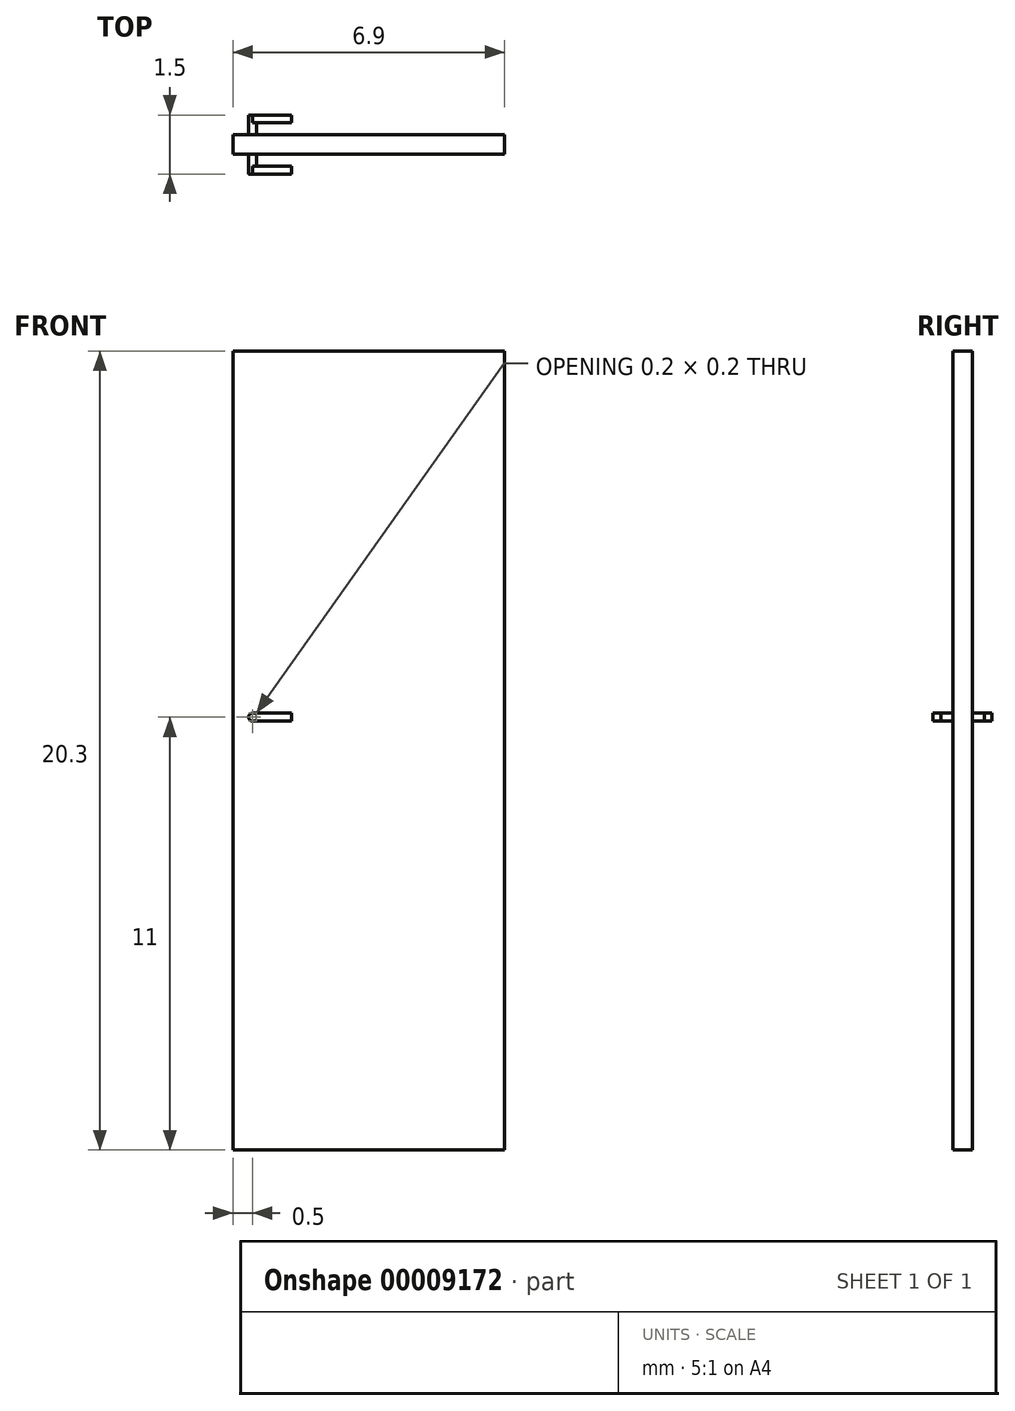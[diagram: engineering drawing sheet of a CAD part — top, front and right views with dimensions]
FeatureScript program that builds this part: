
annotation { "Feature Type Name" : "Feature", "Feature Type Description" : "" }
export const myFeature = defineFeature(function(context is Context, id is Id, definition is map)
    precondition{}
    {
        {
            var Q0;
            Q0=qCreatedBy(makeId("Top.planeOp"),FACE);
            var sketch = newSketch(context, id + "F0", { "sketchPlane" : qUnion([Q0])});
            skLineSegment(sketch, "E0.rect.bottom", {"start": v(3.45, 0.25) * mm, "end": v(-3.45, 0.25) * mm});
            skLineSegment(sketch, "E0.rect.top", {"start": v(3.45, -0.25) * mm, "end": v(-3.45, -0.25) * mm});
            skLineSegment(sketch, "E0.rect.left", {"start": v(3.45, 0.25) * mm, "end": v(3.45, -0.25) * mm});
            skLineSegment(sketch, "E0.rect.right", {"start": v(-3.45, 0.25) * mm, "end": v(-3.45, -0.25) * mm});
            skPoint(sketch, "E0.rect.middle", {"position": v(0, 0) * mm});
            skSolve(sketch);
        }
        {
            var Q0;
            Q0 = qSketchRegion(id + "F0", true);
            extrude(context, id + "F1", {"entities" : qUnion([Q0]), "depth" : 20.3 * mm});
        }
        {
            var Q0;
            Q0=makeQuery(id+"F1.opExtrude","SWEPT_FACE",FACE,{"disambiguationData":[OSD([sQuery(id+"F0.wireOp",EDGE,"E0.rect.top")])]});
            var sketch = newSketch(context, id + "F2", { "sketchPlane" : qUnion([Q0])});
            skCircle(sketch, "E1", {"center": v(-2.95, 11) * mm, "radius": 0.1 * mm});
            skSolve(sketch);
        }
        {
            var Q0;
            Q0 = qSketchRegion(id + "F2", true);
            extrude(context, id + "F3", {"entities" : qUnion([Q0]), "operationType" : NewBodyOperationType.ADD, "depth" : 0.5 * mm});
        }
        {
            var Q0;
            Q0=makeQuery(id+"F3.opExtrude","CAP_FACE",FACE,{"disambiguationData":[OSD([sQuery(id+"F2.wireOp",EDGE,"E1")])],"isStart":false});
            var sketch = newSketch(context, id + "F4", { "sketchPlane" : qUnion([Q0])});
            skLineSegment(sketch, "E2.bottom", {"start": v(-2.95, 11.1) * mm, "end": v(-1.95, 11.1) * mm});
            skLineSegment(sketch, "E2.top", {"start": v(-2.95, 10.9) * mm, "end": v(-1.95, 10.9) * mm});
            skLineSegment(sketch, "E2.left", {"start": v(-2.95, 11.1) * mm, "end": v(-2.95, 10.9) * mm});
            skLineSegment(sketch, "E2.right", {"start": v(-1.95, 11.1) * mm, "end": v(-1.95, 10.9) * mm});
            skSolve(sketch);
        }
        {
            var Q0;
            Q0 = qSketchRegion(id + "F4", true);
            extrude(context, id + "F5", {"entities" : qUnion([Q0]), "operationType" : NewBodyOperationType.ADD, "oppositeDirection" : true, "depth" : 0.2 * mm});
        }
        {
            var Q0;
            Q0=qCreatedBy(makeId("Front.planeOp"),FACE);
            var sketch = newSketch(context, id + "F6", { "sketchPlane" : qUnion([Q0])});
            skLineSegment(sketch, "E3.bottom", {"start": v(-16.2, 19.87) * mm, "end": v(-59.47, 19.87) * mm});
            skLineSegment(sketch, "E3.top", {"start": v(-16.2, -21.93) * mm, "end": v(-59.47, -21.93) * mm});
            skLineSegment(sketch, "E3.left", {"start": v(-16.2, 19.87) * mm, "end": v(-16.2, -21.93) * mm});
            skLineSegment(sketch, "E3.right", {"start": v(-59.47, 19.87) * mm, "end": v(-59.47, -21.93) * mm});
            skSolve(sketch);
        }
        {
            var Q0;
            Q0=makeQuery(id+"F1.opExtrude","SWEPT_BODY",BODY,{"disambiguationData":[OSD([sQuery(id+"F0.wireOp",EDGE,"E0.rect.bottom"),sQuery(id+"F0.wireOp",EDGE,"E0.rect.top"),sQuery(id+"F0.wireOp",EDGE,"E0.rect.left"),sQuery(id+"F0.wireOp",EDGE,"E0.rect.right")])]});
            var Q1;
            Q1=makeQuery(id+"F6.imprint","IMPRINT",FACE,{"disambiguationData":[TD([[makeQuery(id+"F6.imprint","IMPRINT",EDGE,{"derivedFrom":sQuery(id+"F6.wireOp",EDGE,"E3.bottom")}),1.0]])]});
            mirror(context, id + "F7", {"operationType" : NewBodyOperationType.ADD, "entities" : qUnion([Q0]), "mirrorPlane" : qUnion([Q1])});
        }
    });
